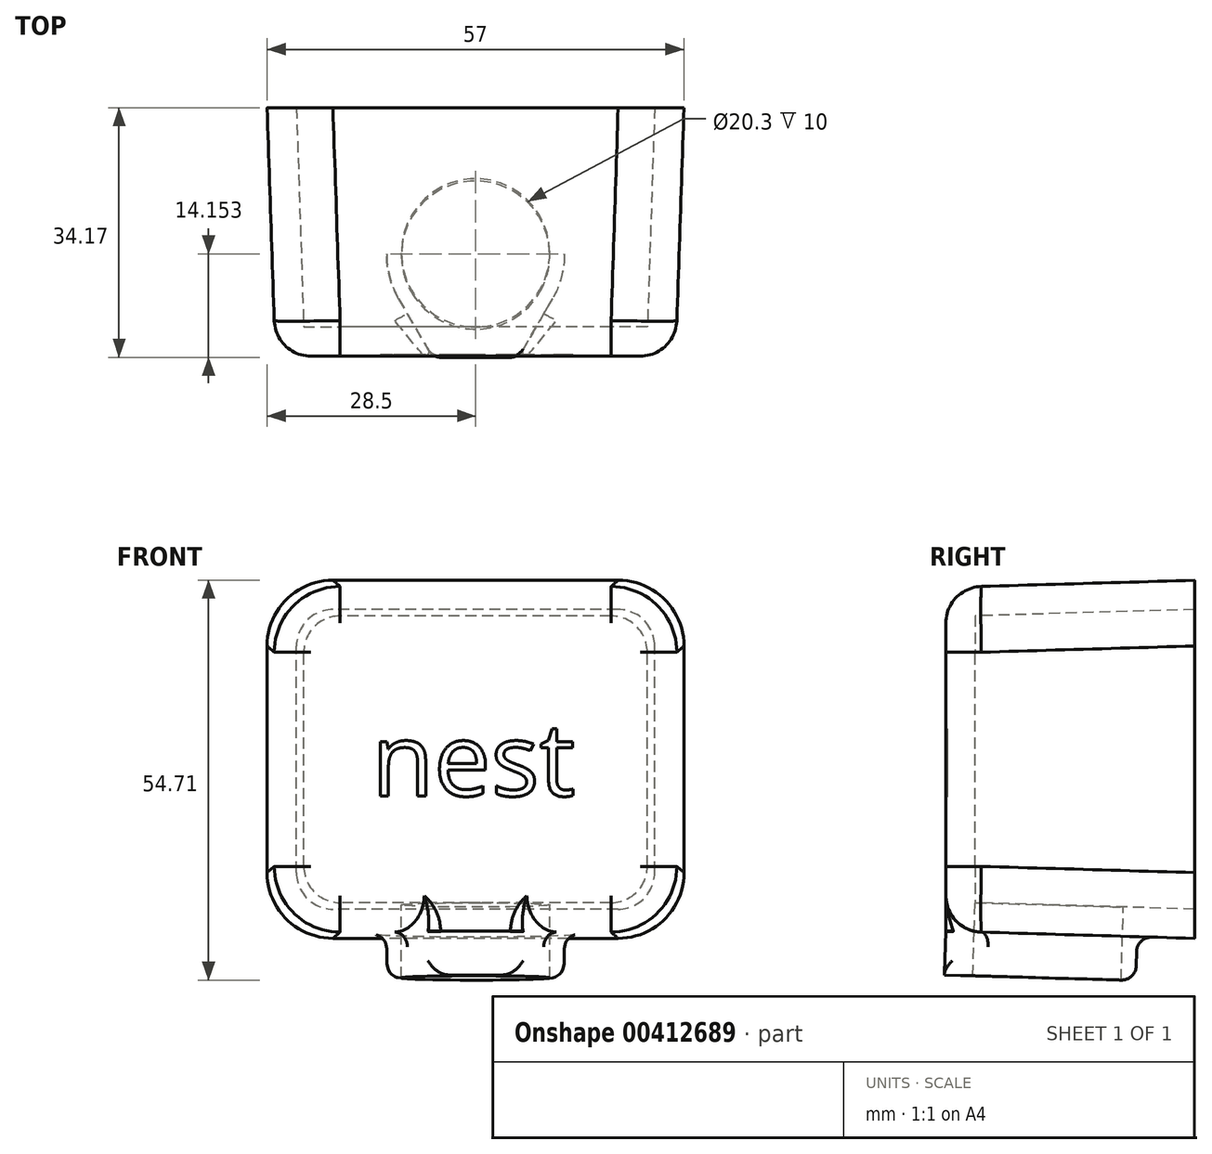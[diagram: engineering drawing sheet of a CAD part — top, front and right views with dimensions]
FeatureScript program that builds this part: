
annotation { "Feature Type Name" : "Feature", "Feature Type Description" : "" }
export const myFeature = defineFeature(function(context is Context, id is Id, definition is map)
    precondition{}
    {
        {
            assignVariable(context, id + "F0", {"name" : "thickness", "anyValue" : 4 * mm});
        }
        {
            var Q0;
            Q0=qCreatedBy(makeId("Front.planeOp"),FACE);
            var sketch = newSketch(context, id + "F1", { "sketchPlane" : qUnion([Q0])});
            skLineSegment(sketch, "E0.bottom", {"start": v(19.5, -20.5) * mm, "end": v(-19.5, -20.5) * mm});
            skLineSegment(sketch, "E0.top", {"start": v(19.5, 20.5) * mm, "end": v(-19.5, 20.5) * mm});
            skLineSegment(sketch, "E0.left", {"start": v(24.5, -15.5) * mm, "end": v(24.5, 15.5) * mm});
            skLineSegment(sketch, "E0.right", {"start": v(-24.5, -15.5) * mm, "end": v(-24.5, 15.5) * mm});
            skPoint(sketch, "E0.middle", {"position": v(0, 0) * mm});
            skPoint(sketch, "E1.visualSharp", {"position": v(-24.5, 20.5) * mm});
            skArc(sketch, "E1.filletArc", {"start": v(-19.5, 20.5) * mm, "mid": v(-23.04, 19.04) * mm, "end": v(-24.5, 15.5) * mm});
            skPoint(sketch, "E2.visualSharp", {"position": v(24.5, 20.5) * mm});
            skArc(sketch, "E2.filletArc", {"start": v(24.5, 15.5) * mm, "mid": v(23.04, 19.04) * mm, "end": v(19.5, 20.5) * mm});
            skPoint(sketch, "E3.visualSharp", {"position": v(24.5, -20.5) * mm});
            skArc(sketch, "E3.filletArc", {"start": v(19.5, -20.5) * mm, "mid": v(23.04, -19.04) * mm, "end": v(24.5, -15.5) * mm});
            skPoint(sketch, "E4.visualSharp", {"position": v(-24.5, -20.5) * mm});
            skArc(sketch, "E4.filletArc", {"start": v(-24.5, -15.5) * mm, "mid": v(-23.04, -19.04) * mm, "end": v(-19.5, -20.5) * mm});
            skSolve(sketch);
        }
        {
            var Q0;
            Q0=qCreatedBy(makeId("Front.planeOp"),FACE);
            cPlane(context, id + "F2", {"entities" : qUnion([Q0]), "cplaneType" : CPlaneType.OFFSET, "offset" : 30 * mm, "width" : 150 * mm, "height" : 150 * mm});
        }
        {
            var Q0;
            Q0=qCreatedBy(id+"F2.planeOp",FACE);
            var sketch = newSketch(context, id + "F3", { "sketchPlane" : qUnion([Q0])});
            skLineSegment(sketch, "E5.bottom", {"start": v(18.5, -19.62) * mm, "end": v(-18.5, -19.63) * mm});
            skLineSegment(sketch, "E5.top", {"start": v(18.5, 19.63) * mm, "end": v(-18.5, 19.62) * mm});
            skLineSegment(sketch, "E5.left", {"start": v(23.5, -14.62) * mm, "end": v(23.5, 14.63) * mm});
            skLineSegment(sketch, "E5.right", {"start": v(-23.5, -14.63) * mm, "end": v(-23.5, 14.62) * mm});
            skPoint(sketch, "E5.middle", {"position": v(0, 0) * mm});
            skPoint(sketch, "E6.visualSharp", {"position": v(-23.5, 19.62) * mm});
            skArc(sketch, "E6.filletArc", {"start": v(-18.5, 19.62) * mm, "mid": v(-22.04, 18.16) * mm, "end": v(-23.5, 14.62) * mm});
            skPoint(sketch, "E7.visualSharp", {"position": v(23.5, 19.63) * mm});
            skArc(sketch, "E7.filletArc", {"start": v(23.5, 14.63) * mm, "mid": v(22.04, 18.16) * mm, "end": v(18.5, 19.63) * mm});
            skPoint(sketch, "E8.visualSharp", {"position": v(23.5, -19.62) * mm});
            skArc(sketch, "E8.filletArc", {"start": v(18.5, -19.62) * mm, "mid": v(22.04, -18.16) * mm, "end": v(23.5, -14.62) * mm});
            skPoint(sketch, "E9.visualSharp", {"position": v(-23.5, -19.63) * mm});
            skArc(sketch, "E9.filletArc", {"start": v(-23.5, -14.63) * mm, "mid": v(-22.04, -18.16) * mm, "end": v(-18.5, -19.63) * mm});
            skSolve(sketch);
        }
        {
            var Q0;
            Q0=makeQuery(id+"F1.imprint","IMPRINT",FACE,{"disambiguationData":[TD([[makeQuery(id+"F1.imprint","IMPRINT",EDGE,{"derivedFrom":sQuery(id+"F1.wireOp",EDGE,"E0.bottom")}),-1.0]])]});
            var Q1;
            Q1=makeQuery(id+"F3.imprint","IMPRINT",FACE,{"disambiguationData":[TD([[makeQuery(id+"F3.imprint","IMPRINT",EDGE,{"derivedFrom":sQuery(id+"F3.wireOp",EDGE,"E5.bottom")}),-1.0]])]});
            loft(context, id + "F4", {"sheetProfilesArray" : [{ "sheetProfileEntities" : qUnion([Q0]) }, { "sheetProfileEntities" : qUnion([Q1]) }]});
        }
        {
            var Q0;
            Q0=makeQuery(id+"F4.opLoft","CAP_FACE",FACE,{"disambiguationData":[OSD([makeQuery(id+"F1.imprint","IMPRINT",FACE,{"disambiguationData":[TD([[makeQuery(id+"F1.imprint","IMPRINT",EDGE,{"derivedFrom":sQuery(id+"F1.wireOp",EDGE,"E0.bottom")}),-1.0]])]})])],"isStart":true});
            shell(context, id + "F5", {"entities" : qUnion([Q0]), "thickness" : getVariable(context, 'thickness'), "oppositeDirection" : true});
        }
        {
            var Q0;
            Q0=makeQuery(id+"F5.opShell","OFFSET_FACE",FACE,{"disambiguationData":[OSD([sQuery(id+"F1.wireOp",EDGE,"E0.bottom"),sQuery(id+"F1.wireOp",EDGE,"E3.filletArc"),sQuery(id+"F1.wireOp",EDGE,"E4.filletArc"),sQuery(id+"F3.wireOp",EDGE,"E5.bottom"),sQuery(id+"F3.wireOp",EDGE,"E8.filletArc"),sQuery(id+"F3.wireOp",EDGE,"E9.filletArc")])]});
            var sketch = newSketch(context, id + "F6", { "sketchPlane" : qUnion([Q0])});
            skCircle(sketch, "E10", {"center": v(0, -19.29) * mm, "radius": 10.15 * mm});
            skSolve(sketch);
        }
        {
            var Q0;
            Q0=makeQuery(id+"F6.imprint","IMPRINT",FACE,{"disambiguationData":[TD([[makeQuery(id+"F6.imprint","IMPRINT",EDGE,{"derivedFrom":sQuery(id+"F6.wireOp",EDGE,"E10")}),-1.0]])]});
            var sketch = newSketch(context, id + "F7", { "sketchPlane" : qUnion([Q0])});
            skCircle(sketch, "E11", {"center": v(0, -19.29) * mm, "radius": 12.15 * mm});
            skSolve(sketch);
        }
        {
            var Q0;
            Q0 = qSketchRegion(id + "F7", true);
            extrude(context, id + "F8", {"entities" : qUnion([Q0]), "operationType" : NewBodyOperationType.ADD, "oppositeDirection" : true, "depth" : 10 * mm});
        }
        {
            var Q0;
            Q0 = qSketchRegion(id + "F6", true);
            extrude(context, id + "F9", {"entities" : qUnion([Q0]), "operationType" : NewBodyOperationType.REMOVE, "endBound" : BoundingType.THROUGH_ALL, "oppositeDirection" : true, "depth" : 25 * mm});
        }
        {
            var Q0;
            Q0=makeQuery(id+"F4.opLoft","SWEPT_FACE",FACE,{"disambiguationData":[OSD([sQuery(id+"F1.wireOp",EDGE,"E0.bottom"),sQuery(id+"F1.wireOp",EDGE,"E3.filletArc"),sQuery(id+"F1.wireOp",EDGE,"E4.filletArc"),sQuery(id+"F3.wireOp",EDGE,"E5.bottom"),sQuery(id+"F3.wireOp",EDGE,"E8.filletArc"),sQuery(id+"F3.wireOp",EDGE,"E9.filletArc")])]});
            var sketch = newSketch(context, id + "F10", { "sketchPlane" : qUnion([Q0])});
            skLineSegment(sketch, "E12", {"start": v(-10.52, 25.36) * mm, "end": v(-5.94, 33.3) * mm});
            skLineSegment(sketch, "E13", {"start": v(10.52, 25.36) * mm, "end": v(5.94, 33.3) * mm});
            skLineSegment(sketch, "E14", {"start": v(-5.94, 33.3) * mm, "end": v(5.94, 33.3) * mm});
            skArc(sketch, "E15", {"start": v(10.52, 25.36) * mm, "mid": v(0, 31.44) * mm, "end": v(-10.52, 25.36) * mm});
            skSolve(sketch);
        }
        {
            var Q0;
            Q0 = qSketchRegion(id + "F10", true);
            var Q1;
            Q1=makeQuery(id+"F8.opExtrude","CAP_FACE",FACE,{"disambiguationData":[OSD([sQuery(id+"F7.wireOp",EDGE,"E11")])],"isStart":false});
            extrude(context, id + "F11", {"entities" : qUnion([Q0]), "operationType" : NewBodyOperationType.ADD, "endBound" : BoundingType.UP_TO_SURFACE, "endBoundEntityFace" : qUnion([Q1]), "depth" : 25 * mm});
        }
        {
            var Q0;
            Q0=makeQuery(id+"F4.opLoft","CAP_FACE",FACE,{"disambiguationData":[OSD([makeQuery(id+"F3.imprint","IMPRINT",FACE,{"disambiguationData":[TD([[makeQuery(id+"F3.imprint","IMPRINT",EDGE,{"derivedFrom":sQuery(id+"F3.wireOp",EDGE,"E5.bottom")}),-1.0]])]})])],"isStart":true});
            var sketch = newSketch(context, id + "F12", { "sketchPlane" : qUnion([Q0])});
            skText(sketch, "E16", { "text": "nest", "fontName": "OpenSans-Regular.ttf"});
            skLineSegment(sketch, "E17", {"start": v(0, 5) * mm, "end": v(0, 23.51) * mm});
            skLineSegment(sketch, "E18", {"start": v(0, -5) * mm, "end": v(0, -23.51) * mm});
            const initialGuessF12  = {"E16": [-0.01423, -0.005, 1, 0, 0.01]};
            skSetInitialGuess(sketch, initialGuessF12);
            skSolve(sketch);
        }
        {
            var Q0;
            Q0 = qSketchRegion(id + "F12", true);
            extrude(context, id + "F13", {"entities" : qUnion([Q0]), "operationType" : NewBodyOperationType.REMOVE, "oppositeDirection" : true, "depth" : 0.2 * mm});
        }
        {
            var Q0;
            Q0=makeQuery(id+"F4.opLoft","MID_CAP_EDGE",EDGE,{"disambiguationData":[OSD([sQuery(id+"F3.wireOp",EDGE,"E5.right"),sQuery(id+"F3.wireOp",EDGE,"E6.filletArc"),sQuery(id+"F3.wireOp",EDGE,"E9.filletArc")])],"capPos":1.0});
            fillet(context, id + "F14", {"entities" : qUnion([Q0]), "radius" : 5 * mm, "tangentPropagation" : true, "allowEdgeOverflow" : false});
        }
        {
            var Q0;
            Q0=makeQuery(id+"F8.boolean.opBoolean","INTERSECT",EDGE,{"derivedFrom":[makeQuery(id+"F4.opLoft","SWEPT_FACE",FACE,{"disambiguationData":[OSD([sQuery(id+"F1.wireOp",EDGE,"E0.bottom"),sQuery(id+"F1.wireOp",EDGE,"E3.filletArc"),sQuery(id+"F1.wireOp",EDGE,"E4.filletArc"),sQuery(id+"F3.wireOp",EDGE,"E5.bottom"),sQuery(id+"F3.wireOp",EDGE,"E8.filletArc"),sQuery(id+"F3.wireOp",EDGE,"E9.filletArc")])]}),makeQuery(id+"F8.opExtrude","SWEPT_FACE",FACE,{"disambiguationData":[OSD([sQuery(id+"F7.wireOp",EDGE,"E11")])]})]});
            var Q1;
            Q1=makeQuery(id+"F11.opExtrude","SWEPT_EDGE",EDGE,{"disambiguationData":[OSD([sQuery(id+"F3.wireOp",EDGE,"E5.bottom"),sQuery(id+"F3.wireOp",EDGE,"E8.filletArc"),sQuery(id+"F3.wireOp",EDGE,"E9.filletArc"),sQuery(id+"F10.wireOp",EDGE,"E12"),sQuery(id+"F10.wireOp",EDGE,"E14")])]});
            var Q2;
            Q2=makeQuery(id+"F11.opExtrude","SWEPT_EDGE",EDGE,{"disambiguationData":[OSD([sQuery(id+"F3.wireOp",EDGE,"E5.bottom"),sQuery(id+"F3.wireOp",EDGE,"E8.filletArc"),sQuery(id+"F3.wireOp",EDGE,"E9.filletArc"),sQuery(id+"F10.wireOp",EDGE,"E13"),sQuery(id+"F10.wireOp",EDGE,"E14")])]});
            var Q3;
            Q3=makeQuery(id+"F8.opExtrude","CAP_EDGE",EDGE,{"disambiguationData":[OSD([sQuery(id+"F7.wireOp",EDGE,"E11")])],"isStart":false});
            var Q4;
            Q4=makeQuery(id+"F11.opExtrude","TWEAK_EDGE",EDGE,{"derivedFrom":[makeQuery(id+"F8.opExtrude","CAP_FACE",FACE,{"disambiguationData":[OSD([sQuery(id+"F7.wireOp",EDGE,"E11")])],"isStart":false}),makeQuery(id+"F10.imprint","IMPRINT",EDGE,{"derivedFrom":sQuery(id+"F10.wireOp",EDGE,"E14")})]});
            fillet(context, id + "F15", {"entities" : qUnion([Q0, Q1, Q2, Q3, Q4]), "radius" : 2 * mm, "tangentPropagation" : true, "allowEdgeOverflow" : false});
        }
    });
